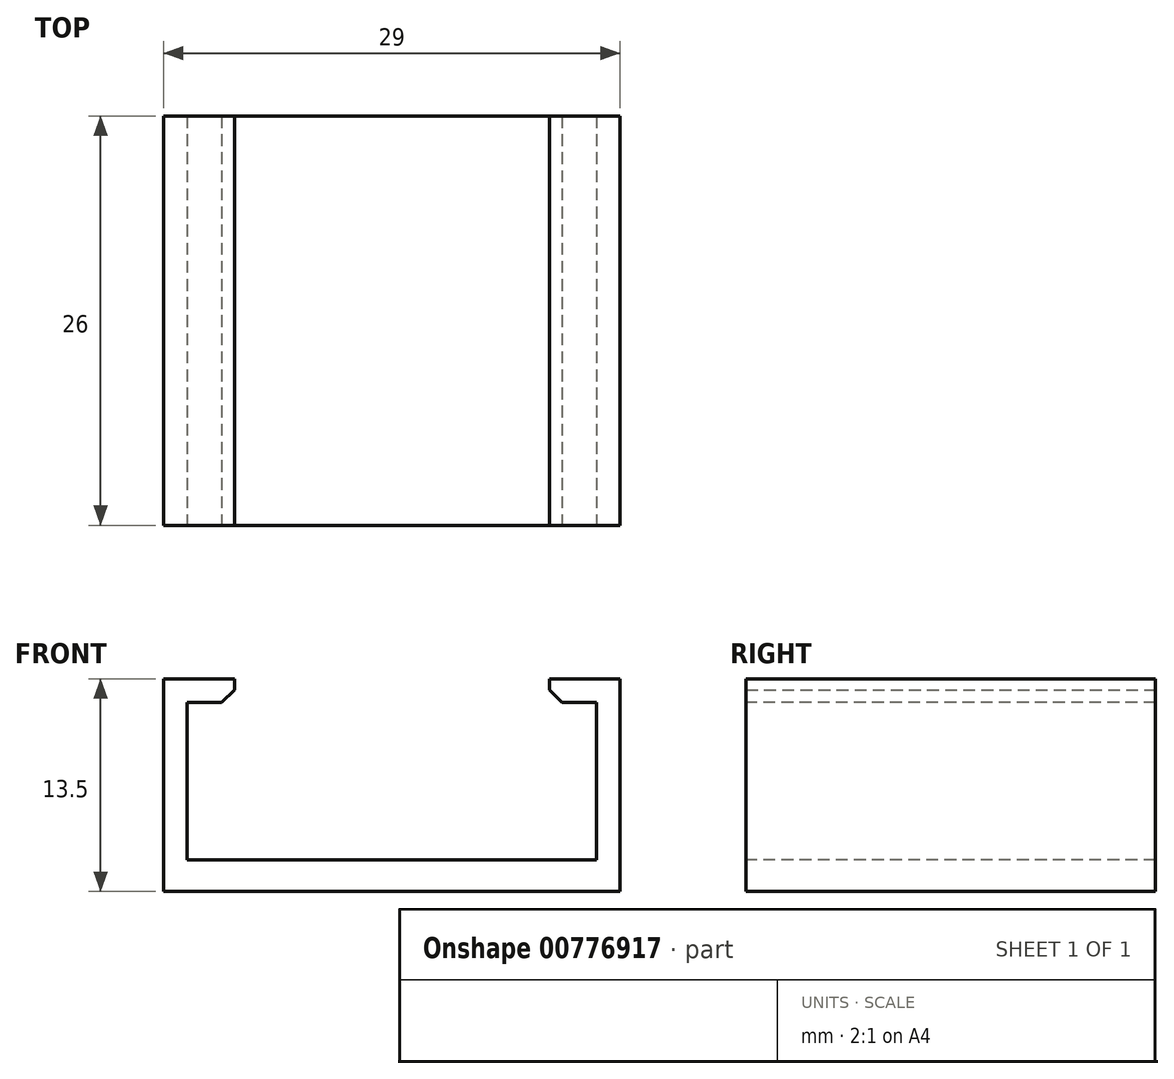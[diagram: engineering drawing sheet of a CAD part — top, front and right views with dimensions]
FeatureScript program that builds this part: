
annotation { "Feature Type Name" : "Feature", "Feature Type Description" : "" }
export const myFeature = defineFeature(function(context is Context, id is Id, definition is map)
    precondition{}
    {
        {
            var Q0;
            Q0=qCreatedBy(makeId("Front.planeOp"),FACE);
            var sketch = newSketch(context, id + "F0", { "sketchPlane" : qUnion([Q0])});
            skLineSegment(sketch, "E0", {"start": v(0, 0) * mm, "end": v(-14.5, 0) * mm});
            skLineSegment(sketch, "E1", {"start": v(-14.5, 0) * mm, "end": v(-14.5, 13.5) * mm});
            skLineSegment(sketch, "E2", {"start": v(-14.5, 13.5) * mm, "end": v(-10, 13.5) * mm});
            skLineSegment(sketch, "E3", {"start": v(-10, 13.5) * mm, "end": v(-10, 12) * mm});
            skLineSegment(sketch, "E4", {"start": v(-10, 12) * mm, "end": v(-13, 12) * mm});
            skLineSegment(sketch, "E5", {"start": v(-13, 12) * mm, "end": v(-13, 2) * mm});
            skLineSegment(sketch, "E6", {"start": v(-13, 2) * mm, "end": v(0, 2) * mm});
            skLineSegment(sketch, "E7", {"start": v(0, 2) * mm, "end": v(0, 0) * mm});
            skSolve(sketch);
        }
        {
            var Q0;
            Q0=makeQuery(id+"F0.imprint","IMPRINT",FACE,{"disambiguationData":[TD([[makeQuery(id+"F0.imprint","IMPRINT",EDGE,{"derivedFrom":sQuery(id+"F0.wireOp",EDGE,"E0")}),-1.0]])]});
            extrude(context, id + "F1", {"entities" : qUnion([Q0]), "oppositeDirection" : true, "depth" : 26 * mm, "offsetDistance" : 25 * mm});
        }
        {
            var Q0;
            Q0=makeQuery(id+"F1.opExtrude","SWEPT_EDGE",EDGE,{"disambiguationData":[OSD([sQuery(id+"F0.wireOp",EDGE,"E3"),sQuery(id+"F0.wireOp",EDGE,"E4")])]});
            chamfer(context, id + "F2", {"entities" : qUnion([Q0]), "width" : 0.8 * mm, "tangentPropagation" : true});
        }
        {
            var Q0;
            Q0=makeQuery(id+"F1.opExtrude","SWEPT_BODY",BODY,{"disambiguationData":[OSD([sQuery(id+"F0.wireOp",EDGE,"E0"),sQuery(id+"F0.wireOp",EDGE,"E1"),sQuery(id+"F0.wireOp",EDGE,"E2"),sQuery(id+"F0.wireOp",EDGE,"E3"),sQuery(id+"F0.wireOp",EDGE,"E4"),sQuery(id+"F0.wireOp",EDGE,"E5"),sQuery(id+"F0.wireOp",EDGE,"E6"),sQuery(id+"F0.wireOp",EDGE,"E7")])]});
            var Q1;
            Q1=qCreatedBy(makeId("Right.planeOp"),FACE);
            mirror(context, id + "F3", {"operationType" : NewBodyOperationType.ADD, "entities" : qUnion([Q0]), "mirrorPlane" : qUnion([Q1])});
        }
    });
